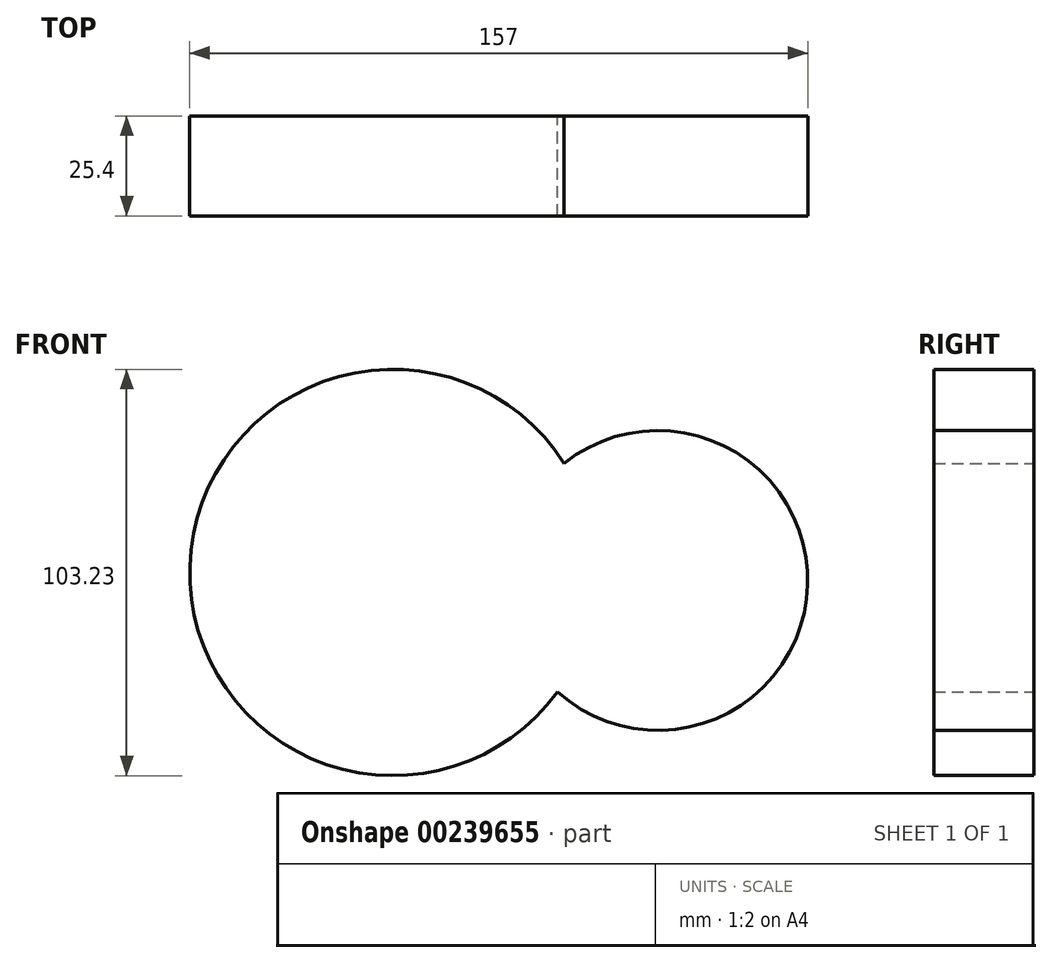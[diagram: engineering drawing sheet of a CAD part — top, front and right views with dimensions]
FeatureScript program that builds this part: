
annotation { "Feature Type Name" : "Feature", "Feature Type Description" : "" }
export const myFeature = defineFeature(function(context is Context, id is Id, definition is map)
    precondition{}
    {
        {
            var Q0;
            Q0=qCreatedBy(makeId("Front.planeOp"),FACE);
            var sketch = newSketch(context, id + "F0", { "sketchPlane" : qUnion([Q0])});
            skCircle(sketch, "E0", {"center": v(0, 0) * mm, "radius": 38.1 * mm});
            skCircle(sketch, "E1", {"center": v(-67.29, 2.03) * mm, "radius": 51.62 * mm});
            skPoint(sketch, "E1.first.point", {"position": v(-16.22, 9.54) * mm});
            skPoint(sketch, "E1.second.point", {"position": v(-29.82, -33.47) * mm});
            skPoint(sketch, "E1.third.point", {"position": v(-54.32, 51.99) * mm});
            skSolve(sketch);
        }
        {
            var Q0;
            {var subQ0=sQuery(id+"F0.wireOp",EDGE,"E1");var subQ1=sQuery(id+"F0.wireOp",EDGE,"E0");var subQ2=makeQuery(id+"F0.imprint","INTERSECT",VERTEX,{"disambiguationData":[OD(0.0)],"derivedFrom":[subQ1,subQ0]});Q0=makeQuery(id+"F0.imprint","IMPRINT",FACE,{"disambiguationData":[TD([[makeQuery(id+"F0.imprint","IMPRINT",EDGE,{"disambiguationData":[TD([[subQ2,-1.0]])],"derivedFrom":subQ1}),1.0]])]});}
            var Q1;
            {var subQ0=sQuery(id+"F0.wireOp",EDGE,"E1");var subQ1=sQuery(id+"F0.wireOp",EDGE,"E0");var subQ2=makeQuery(id+"F0.imprint","INTERSECT",VERTEX,{"disambiguationData":[OD(0.0)],"derivedFrom":[subQ1,subQ0]});Q1=makeQuery(id+"F0.imprint","IMPRINT",FACE,{"disambiguationData":[TD([[makeQuery(id+"F0.imprint","IMPRINT",EDGE,{"disambiguationData":[TD([[subQ2,1.0]])],"derivedFrom":subQ1}),1.0]])]});}
            var Q2;
            {var subQ0=sQuery(id+"F0.wireOp",EDGE,"E1");var subQ1=sQuery(id+"F0.wireOp",EDGE,"E0");var subQ2=makeQuery(id+"F0.imprint","INTERSECT",VERTEX,{"disambiguationData":[OD(0.0)],"derivedFrom":[subQ1,subQ0]});Q2=makeQuery(id+"F0.imprint","IMPRINT",FACE,{"disambiguationData":[TD([[makeQuery(id+"F0.imprint","IMPRINT",EDGE,{"disambiguationData":[TD([[subQ2,1.0]])],"derivedFrom":subQ1}),-1.0]])]});}
            extrude(context, id + "F1", {"entities" : qUnion([Q0, Q1, Q2]), "depth" : 25.4 * mm});
        }
    });
